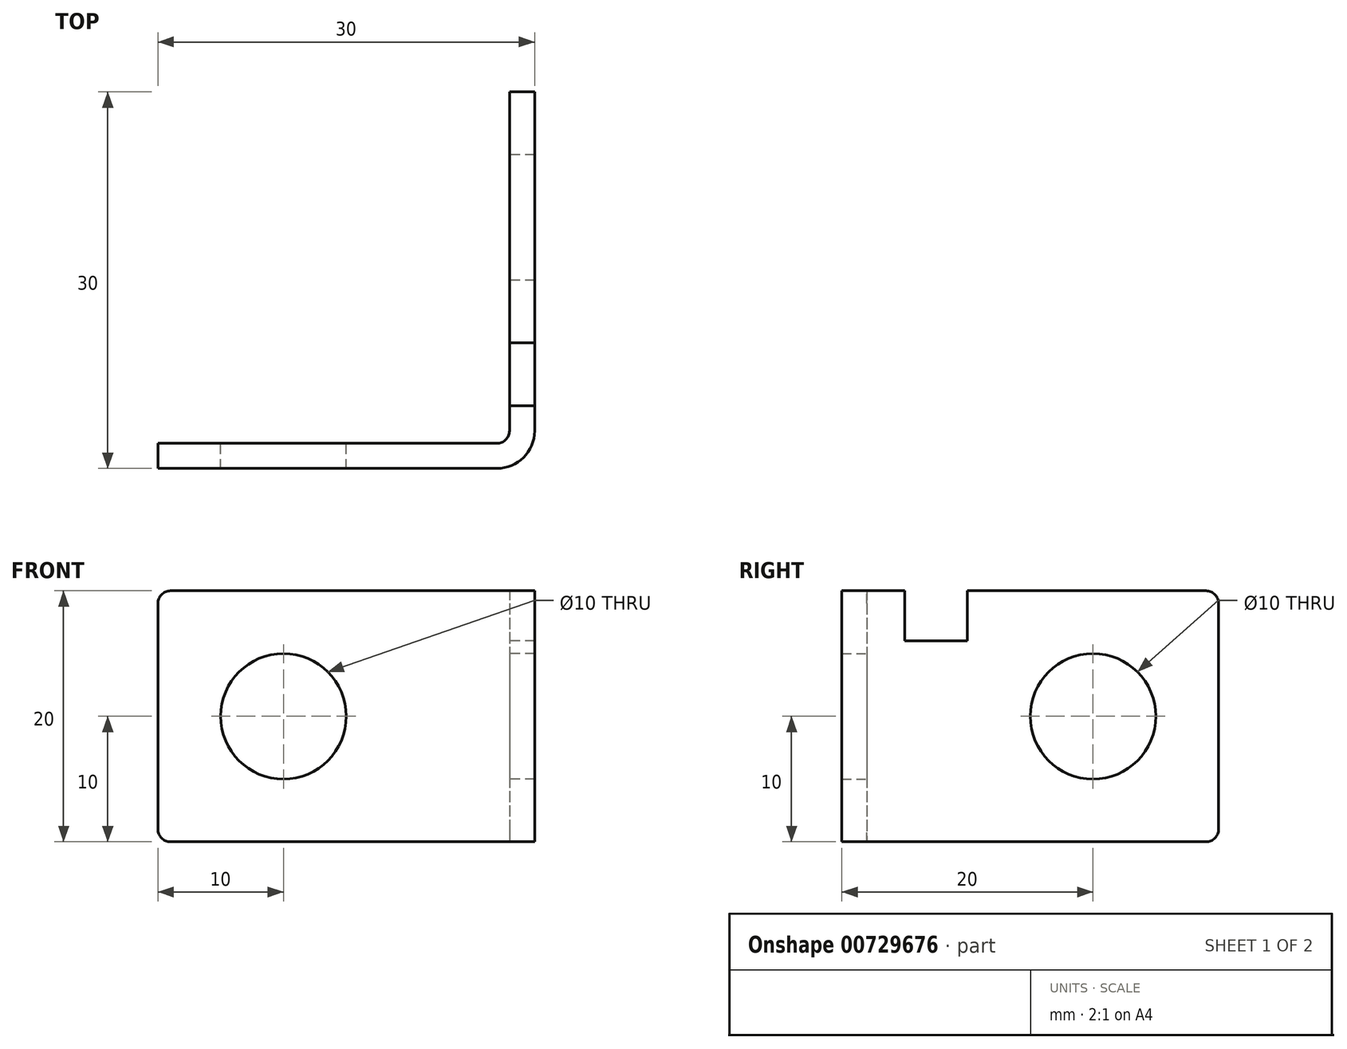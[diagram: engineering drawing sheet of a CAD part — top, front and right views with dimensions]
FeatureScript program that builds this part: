
annotation { "Feature Type Name" : "Feature", "Feature Type Description" : "" }
export const myFeature = defineFeature(function(context is Context, id is Id, definition is map)
    precondition{}
    {
        {
            var Q0;
            Q0=qCreatedBy(makeId("Top.planeOp"),FACE);
            cPlane(context, id + "F0", {"entities" : qUnion([Q0]), "cplaneType" : CPlaneType.OFFSET, "offset" : 0 * mm, "width" : 150 * mm, "height" : 150 * mm});
        }
        {
            var Q0;
            Q0=qCreatedBy(id+"F0.planeOp",FACE);
            var sketch = newSketch(context, id + "F1", { "sketchPlane" : qUnion([Q0])});
            skLineSegment(sketch, "E0", {"start": v(0, 0) * mm, "end": v(0, 1) * mm});
            skLineSegment(sketch, "E1", {"start": v(0, 1) * mm, "end": v(28, 1) * mm});
            skLineSegment(sketch, "E2", {"start": v(0, 0) * mm, "end": v(0, -1) * mm});
            skLineSegment(sketch, "E3", {"start": v(0, -1) * mm, "end": v(30, -1) * mm});
            skLineSegment(sketch, "E4", {"start": v(28, 1) * mm, "end": v(28, 29) * mm});
            skLineSegment(sketch, "E5", {"start": v(28, 29) * mm, "end": v(30, 29) * mm});
            skLineSegment(sketch, "E6", {"start": v(30, 29) * mm, "end": v(30, -1) * mm});
            skPoint(sketch, "E7", {"position": v(29, 29) * mm});
            skPoint(sketch, "E8", {"position": v(2.65, 0) * mm});
            skSolve(sketch);
        }
        {
            var Q0;
            Q0=makeQuery(id+"F1.imprint","IMPRINT",FACE,{"disambiguationData":[TD([[makeQuery(id+"F1.imprint","IMPRINT",EDGE,{"derivedFrom":sQuery(id+"F1.wireOp",EDGE,"E0")}),-1.0]])]});
            extrude(context, id + "F2", {"entities" : qUnion([Q0]), "depth" : 20 * mm, "offsetDistance" : 25 * mm});
        }
        {
            var Q0;
            Q0=makeQuery(id+"F2.opExtrude","CAP_EDGE",EDGE,{"disambiguationData":[OSD([sQuery(id+"F1.wireOp",EDGE,"E0"),sQuery(id+"F1.wireOp",EDGE,"E2")])],"isStart":false});
            var Q1;
            Q1=makeQuery(id+"F2.opExtrude","SWEPT_EDGE",EDGE,{"disambiguationData":[OSD([sQuery(id+"F1.wireOp",EDGE,"E1"),sQuery(id+"F1.wireOp",EDGE,"E4")])]});
            var Q2;
            Q2=makeQuery(id+"F2.opExtrude","CAP_EDGE",EDGE,{"disambiguationData":[OSD([sQuery(id+"F1.wireOp",EDGE,"E5")])],"isStart":true});
            var Q3;
            Q3=makeQuery(id+"F2.opExtrude","CAP_EDGE",EDGE,{"disambiguationData":[OSD([sQuery(id+"F1.wireOp",EDGE,"E5")])],"isStart":false});
            var Q4;
            Q4=makeQuery(id+"F2.opExtrude","CAP_EDGE",EDGE,{"disambiguationData":[OSD([sQuery(id+"F1.wireOp",EDGE,"E0"),sQuery(id+"F1.wireOp",EDGE,"E2")])],"isStart":true});
            fillet(context, id + "F3", {"entities" : qUnion([Q0, Q1, Q2, Q3, Q4]), "radius" : 1 * mm, "tangentPropagation" : true, "allowEdgeOverflow" : false});
        }
        {
            var Q0;
            Q0=makeQuery(id+"F2.opExtrude","SWEPT_EDGE",EDGE,{"disambiguationData":[OSD([sQuery(id+"F1.wireOp",EDGE,"E3"),sQuery(id+"F1.wireOp",EDGE,"E6")])]});
            fillet(context, id + "F4", {"entities" : qUnion([Q0]), "radius" : 3 * mm, "tangentPropagation" : true, "allowEdgeOverflow" : false});
        }
        {
            var Q0;
            Q0=makeQuery(id+"F2.opExtrude","SWEPT_FACE",FACE,{"disambiguationData":[OSD([sQuery(id+"F1.wireOp",EDGE,"E4")])]});
            var sketch = newSketch(context, id + "F5", { "sketchPlane" : qUnion([Q0])});
            skCircle(sketch, "E9", {"center": v(-19, 10) * mm, "radius": 5 * mm});
            skSolve(sketch);
        }
        {
            var Q0;
            Q0 = qSketchRegion(id + "F5", true);
            extrude(context, id + "F6", {"entities" : qUnion([Q0]), "operationType" : NewBodyOperationType.REMOVE, "oppositeDirection" : true, "depth" : 25 * mm, "offsetDistance" : 25 * mm});
        }
        {
            var Q0;
            Q0=makeQuery(id+"F2.opExtrude","SWEPT_FACE",FACE,{"disambiguationData":[OSD([sQuery(id+"F1.wireOp",EDGE,"E1")])]});
            var sketch = newSketch(context, id + "F7", { "sketchPlane" : qUnion([Q0])});
            skCircle(sketch, "E10", {"center": v(-10, 10) * mm, "radius": 5 * mm});
            skSolve(sketch);
        }
        {
            var Q0;
            Q0 = qSketchRegion(id + "F7", true);
            extrude(context, id + "F8", {"entities" : qUnion([Q0]), "operationType" : NewBodyOperationType.REMOVE, "oppositeDirection" : true, "depth" : 25 * mm, "offsetDistance" : 25 * mm});
        }
        {
            var Q0;
            Q0=makeQuery(id+"F2.opExtrude","SWEPT_FACE",FACE,{"disambiguationData":[OSD([sQuery(id+"F1.wireOp",EDGE,"E4")])]});
            var sketch = newSketch(context, id + "F9", { "sketchPlane" : qUnion([Q0])});
            skLineSegment(sketch, "E11.bottom", {"start": v(-9, 20) * mm, "end": v(-4, 20) * mm});
            skLineSegment(sketch, "E11.top", {"start": v(-9, 16) * mm, "end": v(-4, 16) * mm});
            skLineSegment(sketch, "E11.left", {"start": v(-9, 20) * mm, "end": v(-9, 16) * mm});
            skLineSegment(sketch, "E11.right", {"start": v(-4, 20) * mm, "end": v(-4, 16) * mm});
            skSolve(sketch);
        }
        {
            var Q0;
            Q0 = qSketchRegion(id + "F9", true);
            extrude(context, id + "F10", {"entities" : qUnion([Q0]), "operationType" : NewBodyOperationType.REMOVE, "oppositeDirection" : true, "depth" : 25 * mm, "offsetDistance" : 25 * mm});
        }
    });
